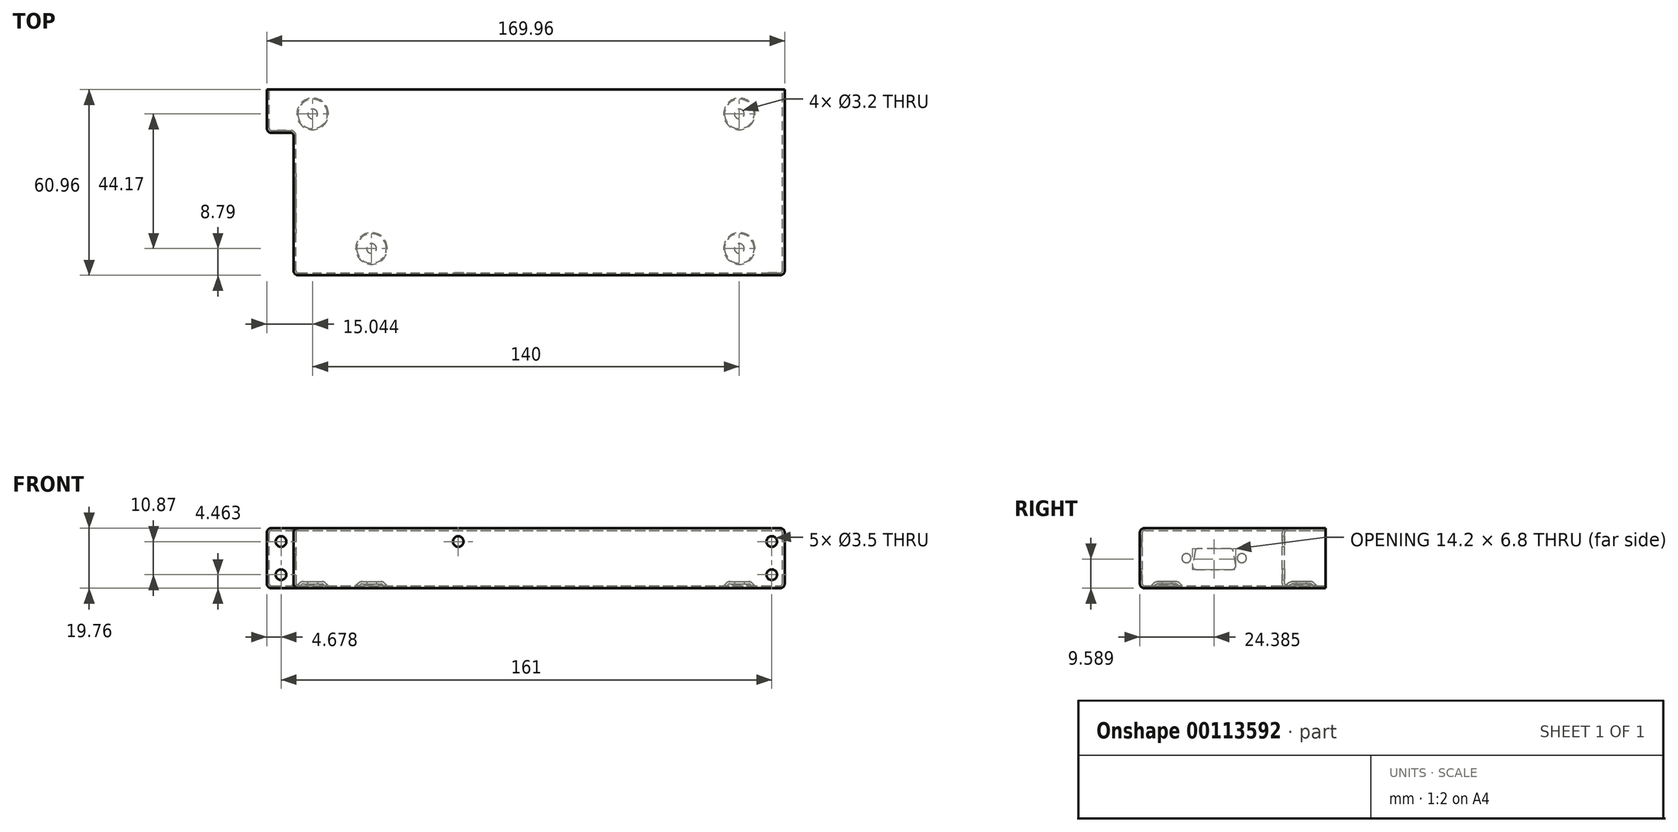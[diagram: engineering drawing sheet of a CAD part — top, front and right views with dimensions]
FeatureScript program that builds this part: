
annotation { "Feature Type Name" : "Feature", "Feature Type Description" : "" }
export const myFeature = defineFeature(function(context is Context, id is Id, definition is map)
    precondition{}
    {
        {
            var Q0;
            Q0=qCreatedBy(makeId("Top.planeOp"),FACE);
            var sketch = newSketch(context, id + "F0", { "sketchPlane" : qUnion([Q0])});
            skLineSegment(sketch, "E0.bottom", {"start": v(-84.98, 0) * mm, "end": v(84.98, 0) * mm});
            skLineSegment(sketch, "E0.top", {"start": v(-76.2, -60.96) * mm, "end": v(84.98, -60.96) * mm});
            skLineSegment(sketch, "E0.left", {"start": v(-84.98, 0) * mm, "end": v(-84.98, -14.22) * mm});
            skLineSegment(sketch, "E0.right", {"start": v(84.98, 0) * mm, "end": v(84.98, -60.96) * mm});
            skLineSegment(sketch, "E1", {"start": v(-76.2, -60.96) * mm, "end": v(-76.2, -14.22) * mm});
            skLineSegment(sketch, "E2", {"start": v(-76.2, -14.22) * mm, "end": v(-84.98, -14.22) * mm});
            skPoint(sketch, "E3.orphan", {"position": v(84.98, -14.22) * mm});
            skSolve(sketch);
        }
        {
            var Q0;
            Q0 = qSketchRegion(id + "F0", true);
            extrude(context, id + "F1", {"entities" : qUnion([Q0]), "oppositeDirection" : true, "depth" : 19.76 * mm});
        }
        {
            var Q0;
            Q0=makeQuery(id+"F1.opExtrude","CAP_FACE",FACE,{"disambiguationData":[OSD([sQuery(id+"F0.wireOp",EDGE,"E0.bottom"),sQuery(id+"F0.wireOp",EDGE,"E0.top"),sQuery(id+"F0.wireOp",EDGE,"E0.left"),sQuery(id+"F0.wireOp",EDGE,"E0.right"),sQuery(id+"F0.wireOp",EDGE,"afNSXiQw-Wu4Q-jcUU-Ve9T-JZMg3j8TVF48"),sQuery(id+"F0.wireOp",EDGE,"0K9XMuOi-Rgmf-rfYT-8b7g-NdUBeN4ZLnnc")])],"isStart":false});
            var sketch = newSketch(context, id + "F2", { "sketchPlane" : qUnion([Q0])});
            skCircle(sketch, "E4", {"center": v(-50.62, 52.17) * mm, "radius": 4.86 * mm});
            skLineSegment(sketch, "E5", {"start": v(-50.62, 52.17) * mm, "end": v(-50.62, 8) * mm, "construction": true});
            skCircle(sketch, "E6", {"center": v(70.06, 8) * mm, "radius": 4.86 * mm});
            skLineSegment(sketch, "E7", {"start": v(-50.62, 52.17) * mm, "end": v(70.06, 52.17) * mm, "construction": true});
            skLineSegment(sketch, "E8", {"start": v(70.06, 52.17) * mm, "end": v(70.06, 8) * mm, "construction": true});
            skLineSegment(sketch, "E9", {"start": v(-50.62, 8) * mm, "end": v(70.06, 8) * mm, "construction": true});
            skCircle(sketch, "E10", {"center": v(70.06, 52.17) * mm, "radius": 4.86 * mm});
            skCircle(sketch, "E11", {"center": v(-69.94, 8) * mm, "radius": 4.86 * mm});
            skSolve(sketch);
        }
        {
            var Q0;
            Q0 = qSketchRegion(id + "F2", true);
            extrude(context, id + "F3", {"entities" : qUnion([Q0]), "operationType" : NewBodyOperationType.REMOVE, "oppositeDirection" : true, "depth" : 1.41 * mm, "hasDraft" : true, "draftAngle" : 45 * degree, "draftPullDirection" : true});
        }
        {
            var Q0;
            Q0=makeQuery(id+"F1.opExtrude","SWEPT_EDGE",EDGE,{"disambiguationData":[OSD([sQuery(id+"F0.wireOp",EDGE,"E1"),sQuery(id+"F0.wireOp",EDGE,"E2")])]});
            var Q1;
            Q1=makeQuery(id+"F3.boolean.opBoolean","COPY",EDGE,{"derivedFrom":makeQuery(id+"F3.opExtrude","CAP_EDGE",EDGE,{"disambiguationData":[OSD([sQuery(id+"F2.wireOp",EDGE,"E11")])],"isStart":false})});
            var Q2;
            Q2=makeQuery(id+"F3.boolean.opBoolean","COPY",EDGE,{"derivedFrom":makeQuery(id+"F3.opExtrude","CAP_EDGE",EDGE,{"disambiguationData":[OSD([sQuery(id+"F2.wireOp",EDGE,"E4")])],"isStart":false})});
            var Q3;
            Q3=makeQuery(id+"F3.boolean.opBoolean","COPY",EDGE,{"derivedFrom":makeQuery(id+"F3.opExtrude","CAP_EDGE",EDGE,{"disambiguationData":[OSD([sQuery(id+"F2.wireOp",EDGE,"E10")])],"isStart":false})});
            var Q4;
            Q4=makeQuery(id+"F3.boolean.opBoolean","COPY",EDGE,{"derivedFrom":makeQuery(id+"F3.opExtrude","CAP_EDGE",EDGE,{"disambiguationData":[OSD([sQuery(id+"F2.wireOp",EDGE,"E6")])],"isStart":false})});
            fillet(context, id + "F4", {"entities" : qUnion([Q0, Q1, Q2, Q3, Q4]), "radius" : 0.8 * mm, "tangentPropagation" : true, "allowEdgeOverflow" : false});
        }
        {
            var Q0;
            Q0=makeQuery(id+"F1.opExtrude","CAP_EDGE",EDGE,{"disambiguationData":[OSD([sQuery(id+"F0.wireOp",EDGE,"E0.right")])],"isStart":false});
            var Q1;
            Q1=makeQuery(id+"F1.opExtrude","CAP_EDGE",EDGE,{"disambiguationData":[OSD([sQuery(id+"F0.wireOp",EDGE,"E0.right")])],"isStart":true});
            var Q2;
            Q2=makeQuery(id+"F1.opExtrude","SWEPT_EDGE",EDGE,{"disambiguationData":[OSD([sQuery(id+"F0.wireOp",EDGE,"E0.top"),sQuery(id+"F0.wireOp",EDGE,"E0.right")])]});
            var Q3;
            Q3=makeQuery(id+"F1.opExtrude","CAP_EDGE",EDGE,{"disambiguationData":[OSD([sQuery(id+"F0.wireOp",EDGE,"E0.top")])],"isStart":false});
            var Q4;
            Q4=makeQuery(id+"F1.opExtrude","CAP_EDGE",EDGE,{"disambiguationData":[OSD([sQuery(id+"F0.wireOp",EDGE,"E0.top")])],"isStart":true});
            var Q5;
            Q5=makeQuery(id+"F1.opExtrude","CAP_EDGE",EDGE,{"disambiguationData":[OSD([sQuery(id+"F0.wireOp",EDGE,"E1")])],"isStart":false});
            var Q6;
            Q6=makeQuery(id+"F1.opExtrude","CAP_EDGE",EDGE,{"disambiguationData":[OSD([sQuery(id+"F0.wireOp",EDGE,"E1")])],"isStart":true});
            var Q7;
            Q7=makeQuery(id+"F1.opExtrude","SWEPT_EDGE",EDGE,{"disambiguationData":[OSD([sQuery(id+"F0.wireOp",EDGE,"E0.top"),sQuery(id+"F0.wireOp",EDGE,"E1")])]});
            var Q8;
            Q8=makeQuery(id+"F1.opExtrude","SWEPT_EDGE",EDGE,{"disambiguationData":[OSD([sQuery(id+"F0.wireOp",EDGE,"E0.left"),sQuery(id+"F0.wireOp",EDGE,"E2")])]});
            var Q9;
            Q9=makeQuery(id+"F1.opExtrude","CAP_EDGE",EDGE,{"disambiguationData":[OSD([sQuery(id+"F0.wireOp",EDGE,"E0.left")])],"isStart":false});
            var Q10;
            Q10=makeQuery(id+"F1.opExtrude","CAP_EDGE",EDGE,{"disambiguationData":[OSD([sQuery(id+"F0.wireOp",EDGE,"E0.left")])],"isStart":true});
            var Q11;
            Q11=makeQuery(id+"F3.boolean.opBoolean","COPY",EDGE,{"derivedFrom":makeQuery(id+"F3.opExtrude","CAP_EDGE",EDGE,{"disambiguationData":[OSD([sQuery(id+"F2.wireOp",EDGE,"E11")])],"isStart":true})});
            var Q12;
            Q12=makeQuery(id+"F3.boolean.opBoolean","COPY",EDGE,{"derivedFrom":makeQuery(id+"F3.opExtrude","CAP_EDGE",EDGE,{"disambiguationData":[OSD([sQuery(id+"F2.wireOp",EDGE,"E4")])],"isStart":true})});
            var Q13;
            Q13=makeQuery(id+"F3.boolean.opBoolean","COPY",EDGE,{"derivedFrom":makeQuery(id+"F3.opExtrude","CAP_EDGE",EDGE,{"disambiguationData":[OSD([sQuery(id+"F2.wireOp",EDGE,"E6")])],"isStart":true})});
            var Q14;
            Q14=makeQuery(id+"F3.boolean.opBoolean","COPY",EDGE,{"derivedFrom":makeQuery(id+"F3.opExtrude","CAP_EDGE",EDGE,{"disambiguationData":[OSD([sQuery(id+"F2.wireOp",EDGE,"E10")])],"isStart":true})});
            fillet(context, id + "F5", {"entities" : qUnion([Q0, Q1, Q2, Q3, Q4, Q5, Q6, Q7, Q8, Q9, Q10, Q11, Q12, Q13, Q14]), "radius" : 1.6 * mm, "tangentPropagation" : true, "allowEdgeOverflow" : false});
        }
        {
            var Q0;
            Q0=makeQuery(id+"F1.opExtrude","SWEPT_FACE",FACE,{"disambiguationData":[OSD([sQuery(id+"F0.wireOp",EDGE,"E0.bottom")])]});
            shell(context, id + "F6", {"entities" : qUnion([Q0]), "thickness" : 0.76 * mm});
        }
        {
            var Q0;
            Q0=makeQuery(id+"F1.opExtrude","CAP_FACE",FACE,{"disambiguationData":[OSD([sQuery(id+"F0.wireOp",EDGE,"E0.bottom"),sQuery(id+"F0.wireOp",EDGE,"E0.top"),sQuery(id+"F0.wireOp",EDGE,"E0.left"),sQuery(id+"F0.wireOp",EDGE,"E0.right"),sQuery(id+"F0.wireOp",EDGE,"afNSXiQw-Wu4Q-jcUU-Ve9T-JZMg3j8TVF48"),sQuery(id+"F0.wireOp",EDGE,"0K9XMuOi-Rgmf-rfYT-8b7g-NdUBeN4ZLnnc")])],"isStart":false});
            var sketch = newSketch(context, id + "F7", { "sketchPlane" : qUnion([Q0])});
            skCircle(sketch, "E12", {"center": v(70.06, 8) * mm, "radius": 1.6 * mm});
            skCircle(sketch, "E13", {"center": v(-69.94, 8) * mm, "radius": 1.6 * mm});
            skCircle(sketch, "E14", {"center": v(70.06, 52.17) * mm, "radius": 1.6 * mm});
            skCircle(sketch, "E15", {"center": v(-50.62, 52.17) * mm, "radius": 1.6 * mm});
            skSolve(sketch);
        }
        {
            var Q0;
            Q0 = qSketchRegion(id + "F7", true);
            var Q1;
            {var subQ0=sQuery(id+"F2.wireOp",EDGE,"E6");Q1=makeQuery(id+"F6.opShell","OFFSET_FACE",FACE,{"disambiguationData":[OSD([subQ0]),TDD([makeQuery(id+"F3.boolean.opBoolean","COPY",FACE,{"derivedFrom":makeQuery(id+"F3.opExtrude","CAP_FACE",FACE,{"disambiguationData":[OSD([subQ0])],"isStart":false})})])]});}
            extrude(context, id + "F8", {"entities" : qUnion([Q0]), "operationType" : NewBodyOperationType.REMOVE, "endBound" : BoundingType.UP_TO_SURFACE, "oppositeDirection" : true, "endBoundEntityFace" : qUnion([Q1]), "depth" : 25 * mm});
        }
        {
            var Q0;
            Q0=makeQuery(id+"F1.opExtrude","SWEPT_FACE",FACE,{"disambiguationData":[OSD([sQuery(id+"F0.wireOp",EDGE,"E0.top")])]});
            var sketch = newSketch(context, id + "F9", { "sketchPlane" : qUnion([Q0])});
            skCircle(sketch, "E16", {"center": v(-80.3, -4.43) * mm, "radius": 1.75 * mm});
            skCircle(sketch, "E17", {"center": v(-80.3, -15.3) * mm, "radius": 1.75 * mm});
            skCircle(sketch, "E18", {"center": v(-22.16, -4.43) * mm, "radius": 1.75 * mm});
            skCircle(sketch, "E19", {"center": v(80.7, -4.43) * mm, "radius": 1.75 * mm});
            skCircle(sketch, "E20", {"center": v(80.7, -15.3) * mm, "radius": 1.75 * mm});
            skLineSegment(sketch, "E21", {"start": v(-80.3, -4.43) * mm, "end": v(80.7, -4.43) * mm, "construction": true});
            skLineSegment(sketch, "E22", {"start": v(-80.3, -15.3) * mm, "end": v(80.7, -15.3) * mm, "construction": true});
            skSolve(sketch);
        }
        {
            var Q0;
            Q0 = qSketchRegion(id + "F9", true);
            var Q1;
            {var subQ0=sQuery(id+"F0.wireOp",EDGE,"afNSXiQw-Wu4Q-jcUU-Ve9T-JZMg3j8TVF48");Q1=makeQuery(id+"F6.opShell","OFFSET_FACE",FACE,{"disambiguationData":[OSD([subQ0]),TDD([makeQuery(id+"F1.opExtrude","SWEPT_FACE",FACE,{"disambiguationData":[OSD([subQ0])]})])]});}
            extrude(context, id + "F10", {"entities" : qUnion([Q0]), "operationType" : NewBodyOperationType.REMOVE, "endBound" : BoundingType.THROUGH_ALL, "oppositeDirection" : true, "endBoundEntityFace" : qUnion([Q1]), "depth" : 25 * mm});
        }
        {
            var Q0;
            Q0=makeQuery(id+"F1.opExtrude","SWEPT_FACE",FACE,{"disambiguationData":[OSD([sQuery(id+"F0.wireOp",EDGE,"E1")])]});
            var sketch = newSketch(context, id + "F11", { "sketchPlane" : qUnion([Q0])});
            skCircle(sketch, "E23", {"center": v(27.48, -9.88) * mm, "radius": 1.5 * mm});
            skCircle(sketch, "E24", {"center": v(45.68, -9.88) * mm, "radius": 1.5 * mm});
            skLineSegment(sketch, "E25", {"start": v(29.5, -12.16) * mm, "end": v(30.3, -7.6) * mm});
            skLineSegment(sketch, "E26", {"start": v(31.28, -6.77) * mm, "end": v(41.87, -6.77) * mm});
            skLineSegment(sketch, "E27", {"start": v(42.85, -7.6) * mm, "end": v(43.66, -12.16) * mm});
            skLineSegment(sketch, "E28", {"start": v(42.48, -13.57) * mm, "end": v(30.68, -13.57) * mm});
            skLineSegment(sketch, "E29", {"start": v(36.58, -6.77) * mm, "end": v(36.58, -13.57) * mm, "construction": true});
            skPoint(sketch, "E30.visualSharp", {"position": v(30.44, -6.77) * mm});
            skArc(sketch, "E30.filletArc", {"start": v(31.28, -6.77) * mm, "mid": v(30.64, -7) * mm, "end": v(30.3, -7.6) * mm});
            skPoint(sketch, "E31.visualSharp", {"position": v(42.7, -6.77) * mm});
            skArc(sketch, "E31.filletArc", {"start": v(42.85, -7.6) * mm, "mid": v(42.5, -7) * mm, "end": v(41.87, -6.77) * mm});
            skPoint(sketch, "E32.visualSharp", {"position": v(29.24, -13.57) * mm});
            skArc(sketch, "E32.filletArc", {"start": v(29.5, -12.16) * mm, "mid": v(29.76, -13.14) * mm, "end": v(30.68, -13.57) * mm});
            skPoint(sketch, "E33.visualSharp", {"position": v(43.9, -13.57) * mm});
            skArc(sketch, "E33.filletArc", {"start": v(42.48, -13.57) * mm, "mid": v(43.4, -13.14) * mm, "end": v(43.66, -12.16) * mm});
            skLineSegment(sketch, "E34.trimOffspring", {"start": v(29.9, -9.88) * mm, "end": v(43.25, -9.88) * mm, "construction": true});
            skSolve(sketch);
        }
        {
            var Q0;
            Q0 = qSketchRegion(id + "F11", true);
            extrude(context, id + "F12", {"entities" : qUnion([Q0]), "operationType" : NewBodyOperationType.REMOVE, "endBound" : BoundingType.UP_TO_NEXT, "oppositeDirection" : true, "depth" : 25 * mm});
        }
    });
